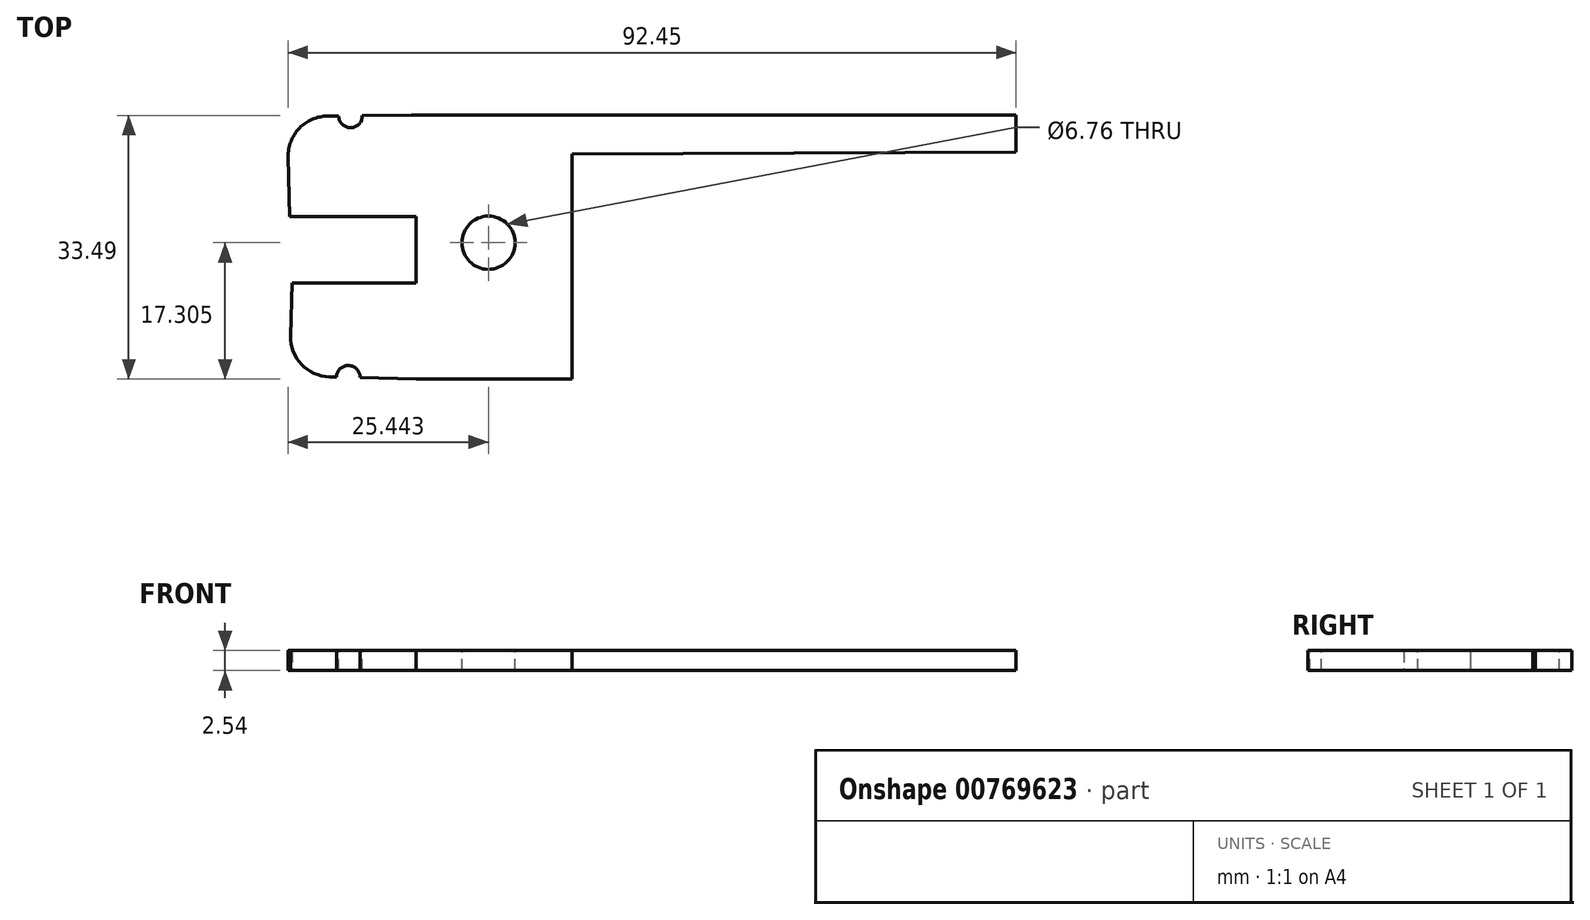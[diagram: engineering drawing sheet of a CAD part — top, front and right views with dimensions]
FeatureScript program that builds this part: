
annotation { "Feature Type Name" : "Feature", "Feature Type Description" : "" }
export const myFeature = defineFeature(function(context is Context, id is Id, definition is map)
    precondition{}
    {
        {
            var Q0;
            Q0=qCreatedBy(makeId("Top.planeOp"),FACE);
            var sketch = newSketch(context, id + "F0", { "sketchPlane" : qUnion([Q0])});
            skLineSegment(sketch, "E0", {"start": v(-26.67, 3.31) * mm, "end": v(-10.61, 3.31) * mm});
            skLineSegment(sketch, "E1", {"start": v(-10.61, 3.31) * mm, "end": v(-10.61, -5.15) * mm});
            skLineSegment(sketch, "E2", {"start": v(-10.61, -5.15) * mm, "end": v(-26.37, -5.15) * mm});
            skLineSegment(sketch, "E3", {"start": v(-26.37, -5.15) * mm, "end": v(-26.67, -16.93) * mm});
            skLineSegment(sketch, "E4", {"start": v(-26.67, -16.93) * mm, "end": v(-10.61, -17.33) * mm});
            skLineSegment(sketch, "E5", {"start": v(-10.61, -17.33) * mm, "end": v(9.25, -17.33) * mm});
            skLineSegment(sketch, "E6", {"start": v(-26.97, 16.03) * mm, "end": v(-26.67, 3.31) * mm});
            skLineSegment(sketch, "E7", {"start": v(-26.97, 16.03) * mm, "end": v(-11.2, 16.16) * mm});
            skLineSegment(sketch, "E8", {"start": v(-11.2, 16.16) * mm, "end": v(65.6, 16.16) * mm});
            skLineSegment(sketch, "E9", {"start": v(65.6, 16.16) * mm, "end": v(65.6, 11.52) * mm});
            skLineSegment(sketch, "E10", {"start": v(9.25, 11.23) * mm, "end": v(65.6, 11.52) * mm});
            skPoint(sketch, "E11.end.orphan", {"position": v(9.25, 3.31) * mm});
            skLineSegment(sketch, "E12", {"start": v(9.25, 11.23) * mm, "end": v(9.25, -17.33) * mm});
            skPoint(sketch, "E13", {"position": v(0, 0) * mm});
            skSolve(sketch);
        }
        {
            var Q0;
            Q0 = qSketchRegion(id + "F0", true);
            extrude(context, id + "F1", {"entities" : qUnion([Q0]), "depth" : 2.54 * mm, "offsetDistance" : 25.4 * mm});
        }
        {
            var Q0;
            Q0=makeQuery(id+"F1.opExtrude","SWEPT_BODY",BODY,{"disambiguationData":[OSD([sQuery(id+"F0.wireOp",EDGE,"E0"),sQuery(id+"F0.wireOp",EDGE,"E1"),sQuery(id+"F0.wireOp",EDGE,"E2"),sQuery(id+"F0.wireOp",EDGE,"E3"),sQuery(id+"F0.wireOp",EDGE,"E4"),sQuery(id+"F0.wireOp",EDGE,"E5"),sQuery(id+"F0.wireOp",EDGE,"E6"),sQuery(id+"F0.wireOp",EDGE,"E7"),sQuery(id+"F0.wireOp",EDGE,"E8"),sQuery(id+"F0.wireOp",EDGE,"E9"),sQuery(id+"F0.wireOp",EDGE,"E10"),sQuery(id+"F0.wireOp",EDGE,"E12")])]});
            transform(context, id + "F2", {"entities" : qUnion([Q0]), "transformType" : TransformType.TRANSLATION_3D, "dx" : -33.78 * mm, "dy" : 26.16 * mm, "dz" : 0 * mm, "makeCopy" : false});
        }
        {
            var Q0;
            Q0=makeQuery(id+"F1.opExtrude","CAP_FACE",FACE,{"disambiguationData":[OSD([sQuery(id+"F0.wireOp",EDGE,"E0"),sQuery(id+"F0.wireOp",EDGE,"E1"),sQuery(id+"F0.wireOp",EDGE,"E2"),sQuery(id+"F0.wireOp",EDGE,"E3"),sQuery(id+"F0.wireOp",EDGE,"E4"),sQuery(id+"F0.wireOp",EDGE,"E5"),sQuery(id+"F0.wireOp",EDGE,"E6"),sQuery(id+"F0.wireOp",EDGE,"E7"),sQuery(id+"F0.wireOp",EDGE,"E8"),sQuery(id+"F0.wireOp",EDGE,"E9"),sQuery(id+"F0.wireOp",EDGE,"E10"),sQuery(id+"F0.wireOp",EDGE,"E12")])],"isStart":false});
            var sketch = newSketch(context, id + "F3", { "sketchPlane" : qUnion([Q0])});
            skPoint(sketch, "E14", {"position": v(-35.19, 26.13) * mm});
            skSolve(sketch);
        }
        {
            var Q0;
            Q0=sQuery(id+"F3.wireOp",VERTEX,"E14");
            var Q1;
            Q1=makeQuery(id+"F1.opExtrude","SWEPT_BODY",BODY,{"disambiguationData":[OSD([sQuery(id+"F0.wireOp",EDGE,"E0"),sQuery(id+"F0.wireOp",EDGE,"E1"),sQuery(id+"F0.wireOp",EDGE,"E2"),sQuery(id+"F0.wireOp",EDGE,"E3"),sQuery(id+"F0.wireOp",EDGE,"E4"),sQuery(id+"F0.wireOp",EDGE,"E5"),sQuery(id+"F0.wireOp",EDGE,"E6"),sQuery(id+"F0.wireOp",EDGE,"E7"),sQuery(id+"F0.wireOp",EDGE,"E8"),sQuery(id+"F0.wireOp",EDGE,"E9"),sQuery(id+"F0.wireOp",EDGE,"E10"),sQuery(id+"F0.wireOp",EDGE,"E12")])]});
            hole(context, id + "F4", {"style" : HoleStyle.SIMPLE, "endStyle" : HoleEndStyle.THROUGH, "standardTappedOrClearance" : lookupTablePath({ "standard" : "ANSI", "fit" : "Normal (ASME)", "size" : "1/4", "type" : "Clearance" }), "standardBlindInLast" : lookupTablePath({ "fit" : "Free", "standard" : "ANSI", "size" : "1/4", "type" : "Clearance" }), "holeDiameter" : 6.76 * mm, "majorDiameter" : 6.35 * mm, "isTappedThrough" : true, "tappedDepth" : 12.7 * mm, "tapClearance" : 3, "locations" : qUnion([Q0]), "scope" : qUnion([Q1])});
        }
        {
            var Q0;
            Q0=makeQuery(id+"F1.opExtrude","SWEPT_EDGE",EDGE,{"disambiguationData":[OSD([sQuery(id+"F0.wireOp",EDGE,"E3"),sQuery(id+"F0.wireOp",EDGE,"E4")])]});
            fillet(context, id + "F5", {"entities" : qUnion([Q0]), "radius" : 5.08 * mm, "tangentPropagation" : true, "allowEdgeOverflow" : false});
        }
        {
            var Q0;
            Q0=makeQuery(id+"F1.opExtrude","SWEPT_EDGE",EDGE,{"disambiguationData":[OSD([sQuery(id+"F0.wireOp",EDGE,"E6"),sQuery(id+"F0.wireOp",EDGE,"E7")])]});
            fillet(context, id + "F6", {"entities" : qUnion([Q0]), "radius" : 5.08 * mm, "tangentPropagation" : true, "allowEdgeOverflow" : false});
        }
        {
            var Q0;
            Q0=makeQuery(id+"F1.opExtrude","CAP_FACE",FACE,{"disambiguationData":[OSD([sQuery(id+"F0.wireOp",EDGE,"E0"),sQuery(id+"F0.wireOp",EDGE,"E1"),sQuery(id+"F0.wireOp",EDGE,"E2"),sQuery(id+"F0.wireOp",EDGE,"E3"),sQuery(id+"F0.wireOp",EDGE,"E4"),sQuery(id+"F0.wireOp",EDGE,"E5"),sQuery(id+"F0.wireOp",EDGE,"E6"),sQuery(id+"F0.wireOp",EDGE,"E7"),sQuery(id+"F0.wireOp",EDGE,"E8"),sQuery(id+"F0.wireOp",EDGE,"E9"),sQuery(id+"F0.wireOp",EDGE,"E10"),sQuery(id+"F0.wireOp",EDGE,"E12")])],"isStart":false});
            var sketch = newSketch(context, id + "F7", { "sketchPlane" : qUnion([Q0])});
            skPoint(sketch, "E15", {"position": v(-52.7, 42.26) * mm});
            skSolve(sketch);
        }
        {
            var Q0;
            Q0=makeQuery(id+"F1.opExtrude","CAP_FACE",FACE,{"disambiguationData":[OSD([sQuery(id+"F0.wireOp",EDGE,"E0"),sQuery(id+"F0.wireOp",EDGE,"E1"),sQuery(id+"F0.wireOp",EDGE,"E2"),sQuery(id+"F0.wireOp",EDGE,"E3"),sQuery(id+"F0.wireOp",EDGE,"E4"),sQuery(id+"F0.wireOp",EDGE,"E5"),sQuery(id+"F0.wireOp",EDGE,"E6"),sQuery(id+"F0.wireOp",EDGE,"E7"),sQuery(id+"F0.wireOp",EDGE,"E8"),sQuery(id+"F0.wireOp",EDGE,"E9"),sQuery(id+"F0.wireOp",EDGE,"E10"),sQuery(id+"F0.wireOp",EDGE,"E12")])],"isStart":false});
            var sketch = newSketch(context, id + "F8", { "sketchPlane" : qUnion([Q0])});
            skPoint(sketch, "E16", {"position": v(-53, 9.04) * mm});
            skSolve(sketch);
        }
        {
            var Q0;
            Q0=sQuery(id+"F7.wireOp",VERTEX,"E15");
            var Q1;
            Q1=makeQuery(id+"F1.opExtrude","SWEPT_BODY",BODY,{"disambiguationData":[OSD([sQuery(id+"F0.wireOp",EDGE,"E0"),sQuery(id+"F0.wireOp",EDGE,"E1"),sQuery(id+"F0.wireOp",EDGE,"E2"),sQuery(id+"F0.wireOp",EDGE,"E3"),sQuery(id+"F0.wireOp",EDGE,"E4"),sQuery(id+"F0.wireOp",EDGE,"E5"),sQuery(id+"F0.wireOp",EDGE,"E6"),sQuery(id+"F0.wireOp",EDGE,"E7"),sQuery(id+"F0.wireOp",EDGE,"E8"),sQuery(id+"F0.wireOp",EDGE,"E9"),sQuery(id+"F0.wireOp",EDGE,"E10"),sQuery(id+"F0.wireOp",EDGE,"E12")])]});
            hole(context, id + "F9", {"style" : HoleStyle.SIMPLE, "endStyle" : HoleEndStyle.THROUGH, "holeDiameter" : 3 * mm, "majorDiameter" : 6.35 * mm, "isTappedThrough" : true, "tappedDepth" : 12.7 * mm, "tapClearance" : 3, "locations" : qUnion([Q0]), "scope" : qUnion([Q1])});
        }
        {
            var Q0;
            Q0=sQuery(id+"F8.wireOp",VERTEX,"E16");
            var Q1;
            Q1=makeQuery(id+"F1.opExtrude","SWEPT_BODY",BODY,{"disambiguationData":[OSD([sQuery(id+"F0.wireOp",EDGE,"E0"),sQuery(id+"F0.wireOp",EDGE,"E1"),sQuery(id+"F0.wireOp",EDGE,"E2"),sQuery(id+"F0.wireOp",EDGE,"E3"),sQuery(id+"F0.wireOp",EDGE,"E4"),sQuery(id+"F0.wireOp",EDGE,"E5"),sQuery(id+"F0.wireOp",EDGE,"E6"),sQuery(id+"F0.wireOp",EDGE,"E7"),sQuery(id+"F0.wireOp",EDGE,"E8"),sQuery(id+"F0.wireOp",EDGE,"E9"),sQuery(id+"F0.wireOp",EDGE,"E10"),sQuery(id+"F0.wireOp",EDGE,"E12")])]});
            hole(context, id + "F10", {"style" : HoleStyle.SIMPLE, "endStyle" : HoleEndStyle.THROUGH, "holeDiameter" : 3 * mm, "majorDiameter" : 6.35 * mm, "isTappedThrough" : true, "tappedDepth" : 12.7 * mm, "tapClearance" : 3, "locations" : qUnion([Q0]), "scope" : qUnion([Q1])});
        }
    });
